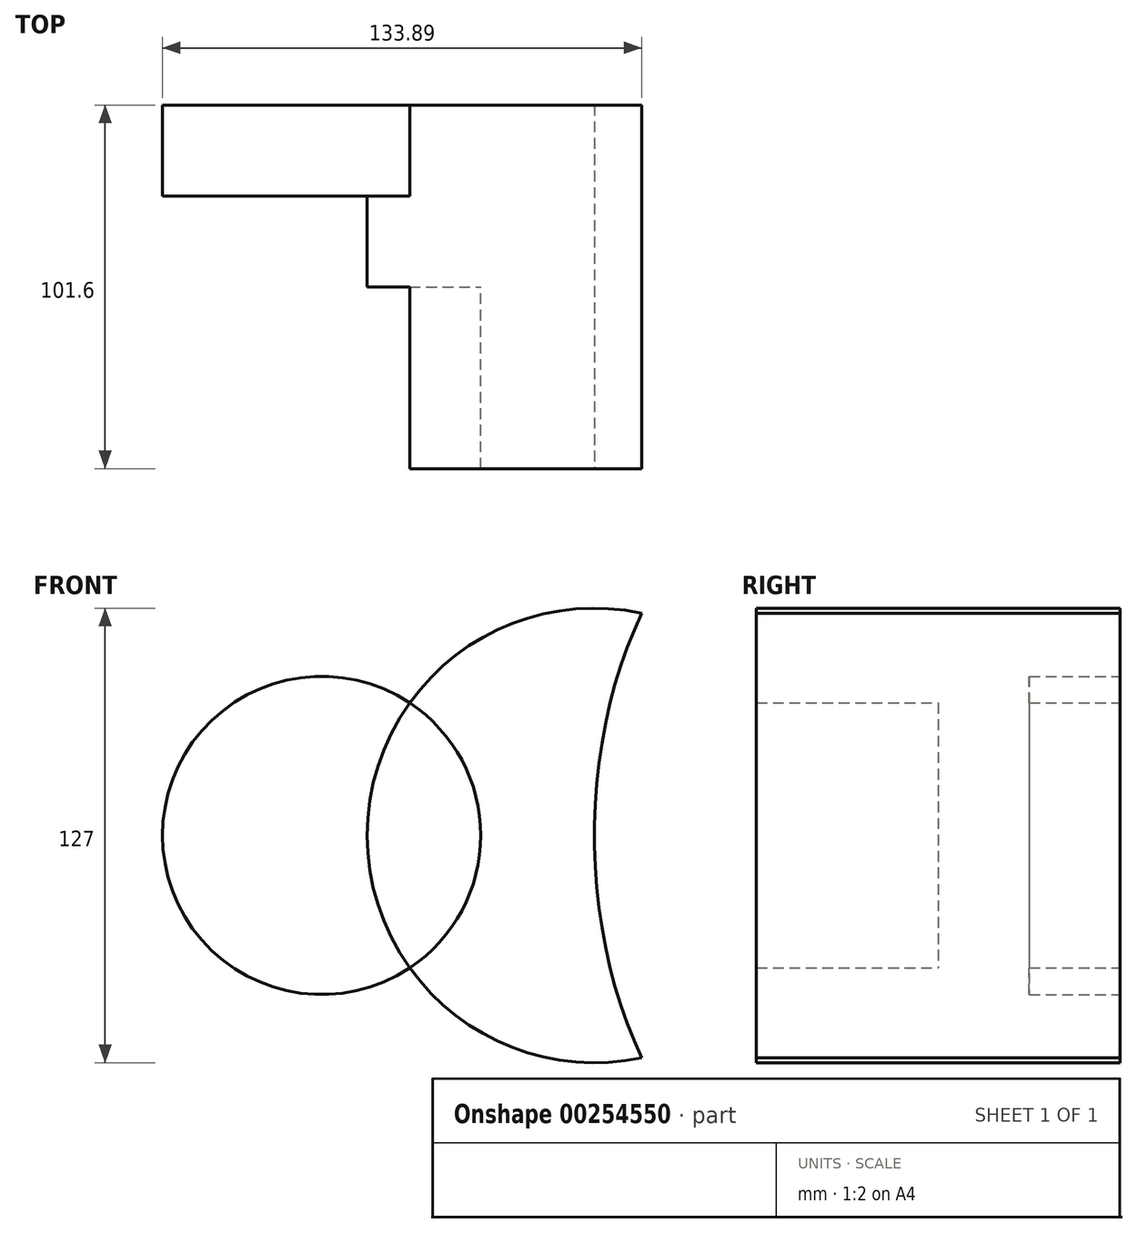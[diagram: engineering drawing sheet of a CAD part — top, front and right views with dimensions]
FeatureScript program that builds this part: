
annotation { "Feature Type Name" : "Feature", "Feature Type Description" : "" }
export const myFeature = defineFeature(function(context is Context, id is Id, definition is map)
    precondition{}
    {
        {
            var Q0;
            Q0=qCreatedBy(makeId("Front.planeOp"),FACE);
            var sketch = newSketch(context, id + "F0", { "sketchPlane" : qUnion([Q0])});
            skCircle(sketch, "E0", {"center": v(-76.2, 0) * mm, "radius": 44.45 * mm});
            skCircle(sketch, "E1", {"center": v(0, 0) * mm, "radius": 63.5 * mm});
            skEllipse(sketch, "E2", {"center": v(63.5, 0) * mm, "majorRadius": 63.5 * mm, "minorRadius": 101.6 * mm, "majorAxis": v(-1, 0)});
            skLineSegment(sketch, "E3", {"start": v(63.5, 0) * mm, "end": v(63.5, 101.6) * mm});
            skSolve(sketch);
        }
        {
            var Q0;
            {var subQ0=sQuery(id+"F0.wireOp",EDGE,"E2");var subQ1=sQuery(id+"F0.wireOp",EDGE,"E1");var subQ2=makeQuery(id+"F0.imprint","INTERSECT",VERTEX,{"disambiguationData":[OD(0.0)],"derivedFrom":[subQ1,subQ0]});Q0=makeQuery(id+"F0.imprint","IMPRINT",FACE,{"disambiguationData":[TD([[makeQuery(id+"F0.imprint","IMPRINT",EDGE,{"disambiguationData":[TD([[subQ2,1.0]])],"derivedFrom":subQ1}),-1.0]])]});}
            var Q1;
            {var subQ0=sQuery(id+"F0.wireOp",EDGE,"E2");var subQ1=sQuery(id+"F0.wireOp",EDGE,"E1");var subQ2=makeQuery(id+"F0.imprint","INTERSECT",VERTEX,{"disambiguationData":[OD(0.0)],"derivedFrom":[subQ1,subQ0]});Q1=makeQuery(id+"F0.imprint","IMPRINT",FACE,{"disambiguationData":[TD([[makeQuery(id+"F0.imprint","IMPRINT",EDGE,{"disambiguationData":[TD([[subQ2,1.0]])],"derivedFrom":subQ1}),1.0]])]});}
            extrude(context, id + "F1", {"entities" : qUnion([Q0, Q1]), "depth" : 101.6 * mm});
        }
        {
            var Q0;
            {var subQ0=sQuery(id+"F0.wireOp",EDGE,"E1");var subQ1=sQuery(id+"F0.wireOp",EDGE,"E0");var subQ2=makeQuery(id+"F0.imprint","INTERSECT",VERTEX,{"disambiguationData":[OD(0.0)],"derivedFrom":[subQ1,subQ0]});Q0=makeQuery(id+"F0.imprint","IMPRINT",FACE,{"disambiguationData":[TD([[makeQuery(id+"F0.imprint","IMPRINT",EDGE,{"disambiguationData":[TD([[subQ2,1.0]])],"derivedFrom":subQ1}),-1.0]])]});}
            var Q1;
            {var subQ0=sQuery(id+"F0.wireOp",EDGE,"E1");var subQ1=sQuery(id+"F0.wireOp",EDGE,"E0");var subQ2=makeQuery(id+"F0.imprint","INTERSECT",VERTEX,{"disambiguationData":[OD(0.0)],"derivedFrom":[subQ1,subQ0]});Q1=makeQuery(id+"F0.imprint","IMPRINT",FACE,{"disambiguationData":[TD([[makeQuery(id+"F0.imprint","IMPRINT",EDGE,{"disambiguationData":[TD([[subQ2,1.0]])],"derivedFrom":subQ1}),1.0]])]});}
            extrude(context, id + "F2", {"entities" : qUnion([Q0, Q1]), "operationType" : NewBodyOperationType.ADD, "depth" : 50.8 * mm});
        }
        {
            var Q0;
            {var subQ0=sQuery(id+"F0.wireOp",EDGE,"E1");var subQ1=sQuery(id+"F0.wireOp",EDGE,"E0");var subQ2=makeQuery(id+"F0.imprint","INTERSECT",VERTEX,{"disambiguationData":[OD(0.0)],"derivedFrom":[subQ1,subQ0]});Q0=makeQuery(id+"F0.imprint","IMPRINT",FACE,{"disambiguationData":[TD([[makeQuery(id+"F0.imprint","IMPRINT",EDGE,{"disambiguationData":[TD([[subQ2,-1.0]])],"derivedFrom":subQ1}),1.0]])]});}
            extrude(context, id + "F3", {"entities" : qUnion([Q0]), "operationType" : NewBodyOperationType.ADD, "depth" : 25.4 * mm});
        }
    });
